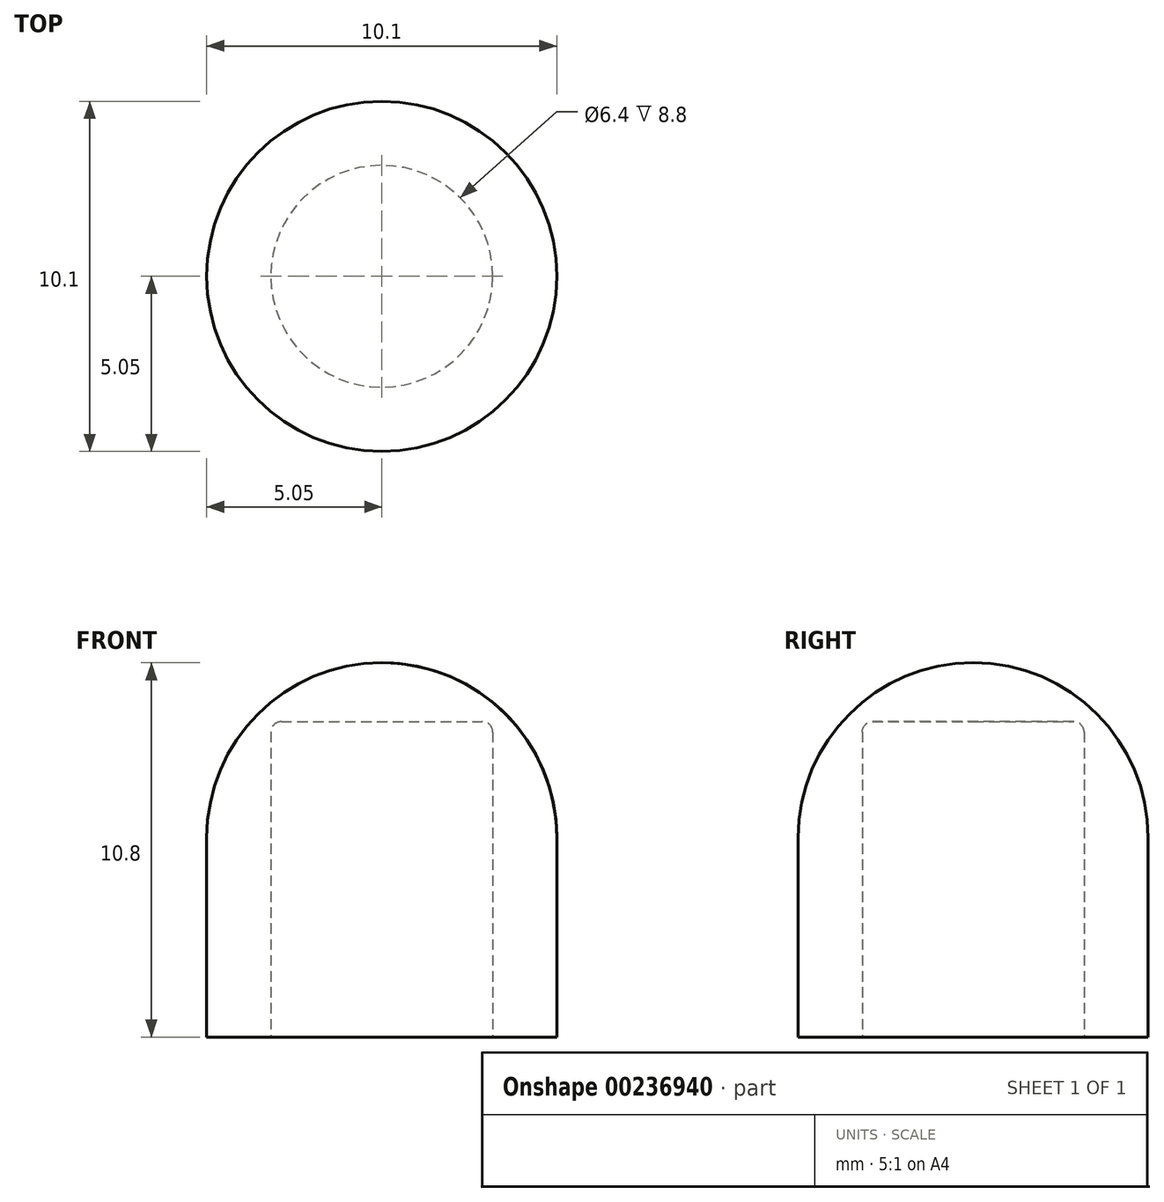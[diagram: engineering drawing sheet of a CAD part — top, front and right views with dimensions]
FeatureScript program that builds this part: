
annotation { "Feature Type Name" : "Feature", "Feature Type Description" : "" }
export const myFeature = defineFeature(function(context is Context, id is Id, definition is map)
    precondition{}
    {
        {
            var Q0;
            Q0=qCreatedBy(makeId("Top.planeOp"),FACE);
            var sketch = newSketch(context, id + "F0", { "sketchPlane" : qUnion([Q0])});
            skCircle(sketch, "E0", {"center": v(0, 0) * mm, "radius": 5.05 * mm});
            skSolve(sketch);
        }
        {
            var Q0;
            Q0=qSketchRegion(id+"F0",true);
            extrude(context, id + "F1", {"entities" : qUnion([Q0]), "depth" : 10.8 * mm});
        }
        {
            var Q0;
            Q0=makeQuery(id+"F1.opExtrude","CAP_EDGE",EDGE,{"disambiguationData":[OSD([sQuery(id+"F0.wireOp",EDGE,"E0")])],"isStart":false});
            fillet(context, id + "F2", {"entities" : qUnion([Q0]), "radius" : 5.05 * mm, "tangentPropagation" : true, "allowEdgeOverflow" : false});
        }
        {
            var Q0;
            Q0=makeQuery(id+"F1.opExtrude","CAP_FACE",FACE,{"disambiguationData":[OSD([sQuery(id+"F0.wireOp",EDGE,"E0")])],"isStart":true});
            var sketch = newSketch(context, id + "F3", { "sketchPlane" : qUnion([Q0])});
            skCircle(sketch, "E1", {"center": v(0, 0) * mm, "radius": 3.2 * mm});
            skSolve(sketch);
        }
        {
            var Q0;
            Q0=makeQuery(id+"F3.imprint","IMPRINT",FACE,{"disambiguationData":[TD([[makeQuery(id+"F3.imprint","IMPRINT",EDGE,{"derivedFrom":sQuery(id+"F3.wireOp",EDGE,"E1")}),1.0]])]});
            extrude(context, id + "F4", {"entities" : qUnion([Q0]), "operationType" : NewBodyOperationType.REMOVE, "oppositeDirection" : true, "depth" : 9.1 * mm});
        }
        {
            var Q0;
            Q0=makeQuery(id+"F4.boolean.opBoolean","COPY",EDGE,{"derivedFrom":makeQuery(id+"F4.opExtrude","CAP_EDGE",EDGE,{"disambiguationData":[OSD([sQuery(id+"F3.wireOp",EDGE,"E1")])],"isStart":false})});
            fillet(context, id + "F5", {"entities" : qUnion([Q0]), "radius" : 0.3 * mm, "tangentPropagation" : true, "allowEdgeOverflow" : false});
        }
    });
